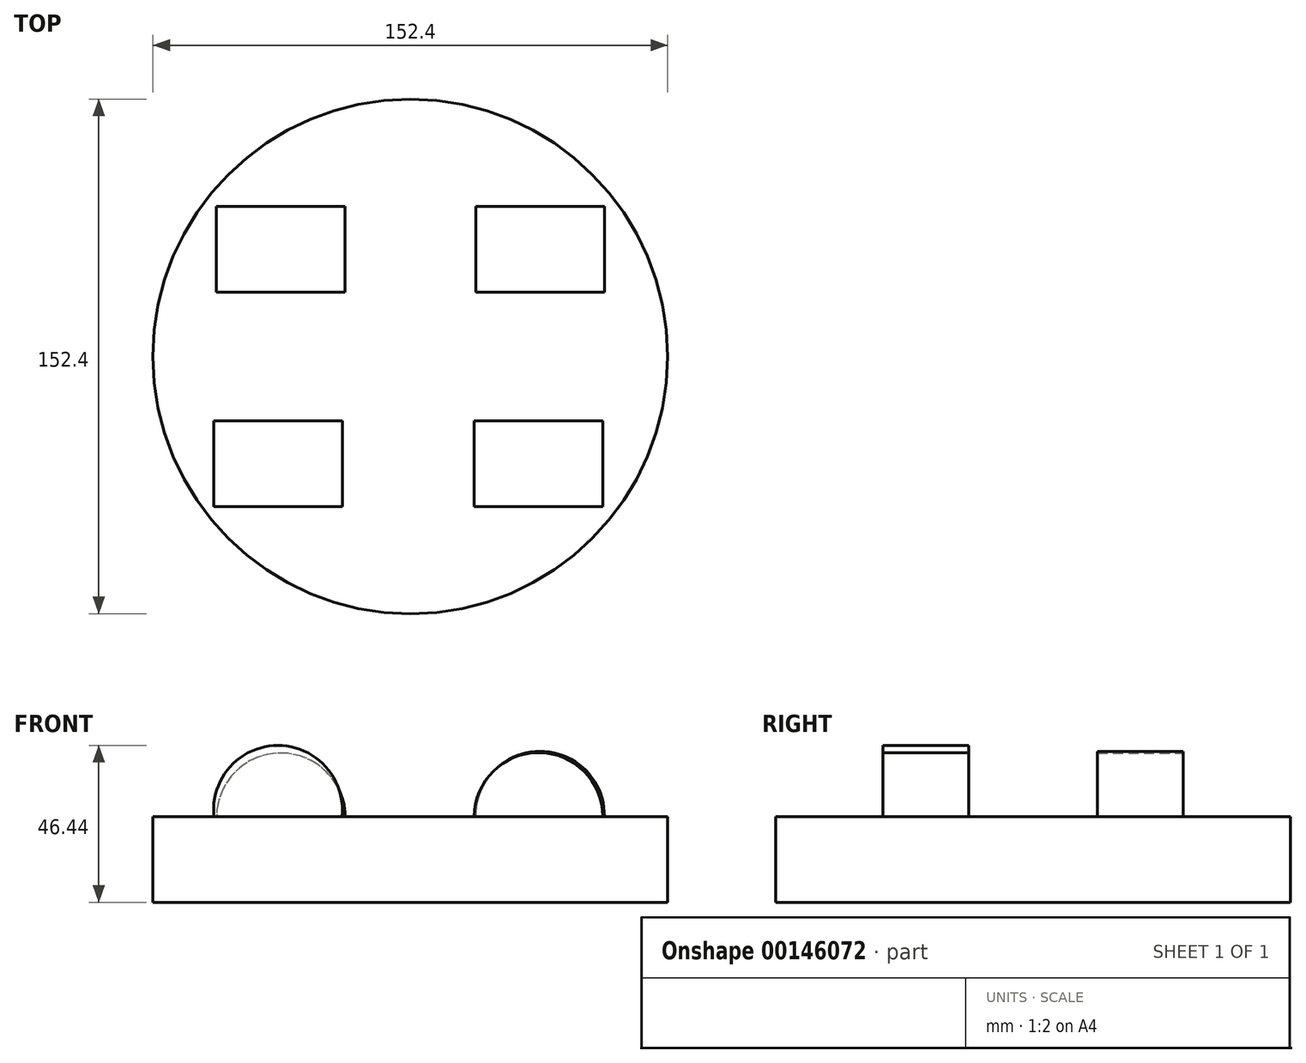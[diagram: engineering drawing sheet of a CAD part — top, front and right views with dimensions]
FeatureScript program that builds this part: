
annotation { "Feature Type Name" : "Feature", "Feature Type Description" : "" }
export const myFeature = defineFeature(function(context is Context, id is Id, definition is map)
    precondition{}
    {
        {
            var Q0;
            Q0=qCreatedBy(makeId("Top.planeOp"),FACE);
            var sketch = newSketch(context, id + "F0", { "sketchPlane" : qUnion([Q0])});
            skCircle(sketch, "E0", {"center": v(0, 0) * mm, "radius": 76.2 * mm});
            skSolve(sketch);
        }
        {
            var Q0;
            Q0 = qSketchRegion(id + "F0", true);
            extrude(context, id + "F1", {"entities" : qUnion([Q0]), "depth" : 25.4 * mm});
        }
        {
            var Q0;
            Q0=makeQuery(id+"F1.opExtrude","CAP_FACE",FACE,{"disambiguationData":[OSD([sQuery(id+"F0.wireOp",EDGE,"E0")])],"isStart":false});
            var sketch = newSketch(context, id + "F2", { "sketchPlane" : qUnion([Q0])});
            skPoint(sketch, "E1", {"position": v(0, 0) * mm});
            skLineSegment(sketch, "E2", {"start": v(0, 0) * mm, "end": v(38.1, 0) * mm});
            skLineSegment(sketch, "E3", {"start": v(0, 0) * mm, "end": v(-38.1, 0) * mm});
            skLineSegment(sketch, "E4", {"start": v(-38.1, 0) * mm, "end": v(-38.1, -31.75) * mm});
            skLineSegment(sketch, "E5", {"start": v(-38.1, 0) * mm, "end": v(-38.1, 31.75) * mm});
            skLineSegment(sketch, "E6", {"start": v(38.1, 0) * mm, "end": v(38.1, -31.75) * mm});
            skLineSegment(sketch, "E7", {"start": v(38.1, 0) * mm, "end": v(38.1, 31.75) * mm});
            skPoint(sketch, "E8", {"position": v(38.1, -31.75) * mm});
            skPoint(sketch, "E9", {"position": v(38.1, 31.75) * mm});
            skPoint(sketch, "E10", {"position": v(-38.1, -31.75) * mm});
            skPoint(sketch, "E11", {"position": v(-38.1, 31.75) * mm});
            skSolve(sketch);
        }
        {
            var Q0;
            Q0=sQuery(id+"F2.wireOp",VERTEX,"E9");
            var Q1;
            Q1=qCreatedBy(makeId("Front.planeOp"),FACE);
            cPlane(context, id + "F3", {"entities" : qUnion([Q0, Q1]), "cplaneType" : CPlaneType.PLANE_POINT, "offset" : 25.4 * mm, "width" : 152.4 * mm, "height" : 152.4 * mm});
        }
        {
            var Q0;
            Q0=qCreatedBy(id+"F3.planeOp",FACE);
            var sketch = newSketch(context, id + "F4", { "sketchPlane" : qUnion([Q0])});
            skPoint(sketch, "E12", {"position": v(38.42, 25.64) * mm});
            skCircle(sketch, "E13", {"center": v(38.42, 25.64) * mm, "radius": 19.05 * mm});
            skSolve(sketch);
        }
        {
            var Q0;
            Q0 = qSketchRegion(id + "F4", true);
            extrude(context, id + "F5", {"entities" : qUnion([Q0]), "operationType" : NewBodyOperationType.ADD, "endBound" : BoundingType.SYMMETRIC, "depth" : 25.4 * mm});
        }
        {
            var Q0;
            Q0=sQuery(id+"F2.wireOp",VERTEX,"E8");
            var Q1;
            Q1=qCreatedBy(makeId("Front.planeOp"),FACE);
            cPlane(context, id + "F6", {"entities" : qUnion([Q0, Q1]), "cplaneType" : CPlaneType.PLANE_POINT, "offset" : 25.4 * mm, "width" : 152.4 * mm, "height" : 152.4 * mm});
        }
        {
            var Q0;
            Q0=qCreatedBy(id+"F6.planeOp",FACE);
            var sketch = newSketch(context, id + "F7", { "sketchPlane" : qUnion([Q0])});
            skPoint(sketch, "E14", {"position": v(40.73, 0) * mm});
            skPoint(sketch, "E15", {"position": v(0, -98.17) * mm});
            skPoint(sketch, "E16", {"position": v(40.73, 27.65) * mm});
            skPoint(sketch, "E17", {"position": v(37.97, 27.65) * mm});
            skPoint(sketch, "E18", {"position": v(37.97, 25.26) * mm});
            skCircle(sketch, "E19", {"center": v(37.97, 25.26) * mm, "radius": 19.05 * mm});
            skSolve(sketch);
        }
        {
            var Q0;
            Q0 = qSketchRegion(id + "F7", true);
            extrude(context, id + "F8", {"entities" : qUnion([Q0]), "operationType" : NewBodyOperationType.ADD, "endBound" : BoundingType.SYMMETRIC, "depth" : 25.4 * mm});
        }
        {
            var Q0;
            Q0=qCreatedBy(id+"F3.planeOp",FACE);
            var sketch = newSketch(context, id + "F9", { "sketchPlane" : qUnion([Q0])});
            skPoint(sketch, "E20", {"position": v(-38.33, 25.15) * mm});
            skCircle(sketch, "E21", {"center": v(-38.33, 25.15) * mm, "radius": 19.05 * mm});
            skSolve(sketch);
        }
        {
            var Q0;
            Q0 = qSketchRegion(id + "F9", true);
            extrude(context, id + "F10", {"entities" : qUnion([Q0]), "operationType" : NewBodyOperationType.ADD, "endBound" : BoundingType.SYMMETRIC, "depth" : 25.4 * mm});
        }
        {
            var Q0;
            Q0=qCreatedBy(id+"F6.planeOp",FACE);
            var sketch = newSketch(context, id + "F11", { "sketchPlane" : qUnion([Q0])});
            skPoint(sketch, "E22", {"position": v(-39.2, 27.39) * mm});
            skCircle(sketch, "E23", {"center": v(-39.2, 27.39) * mm, "radius": 19.05 * mm});
            skSolve(sketch);
        }
        {
            var Q0;
            Q0 = qSketchRegion(id + "F11", true);
            extrude(context, id + "F12", {"entities" : qUnion([Q0]), "operationType" : NewBodyOperationType.ADD, "endBound" : BoundingType.SYMMETRIC, "depth" : 25.4 * mm});
        }
    });
